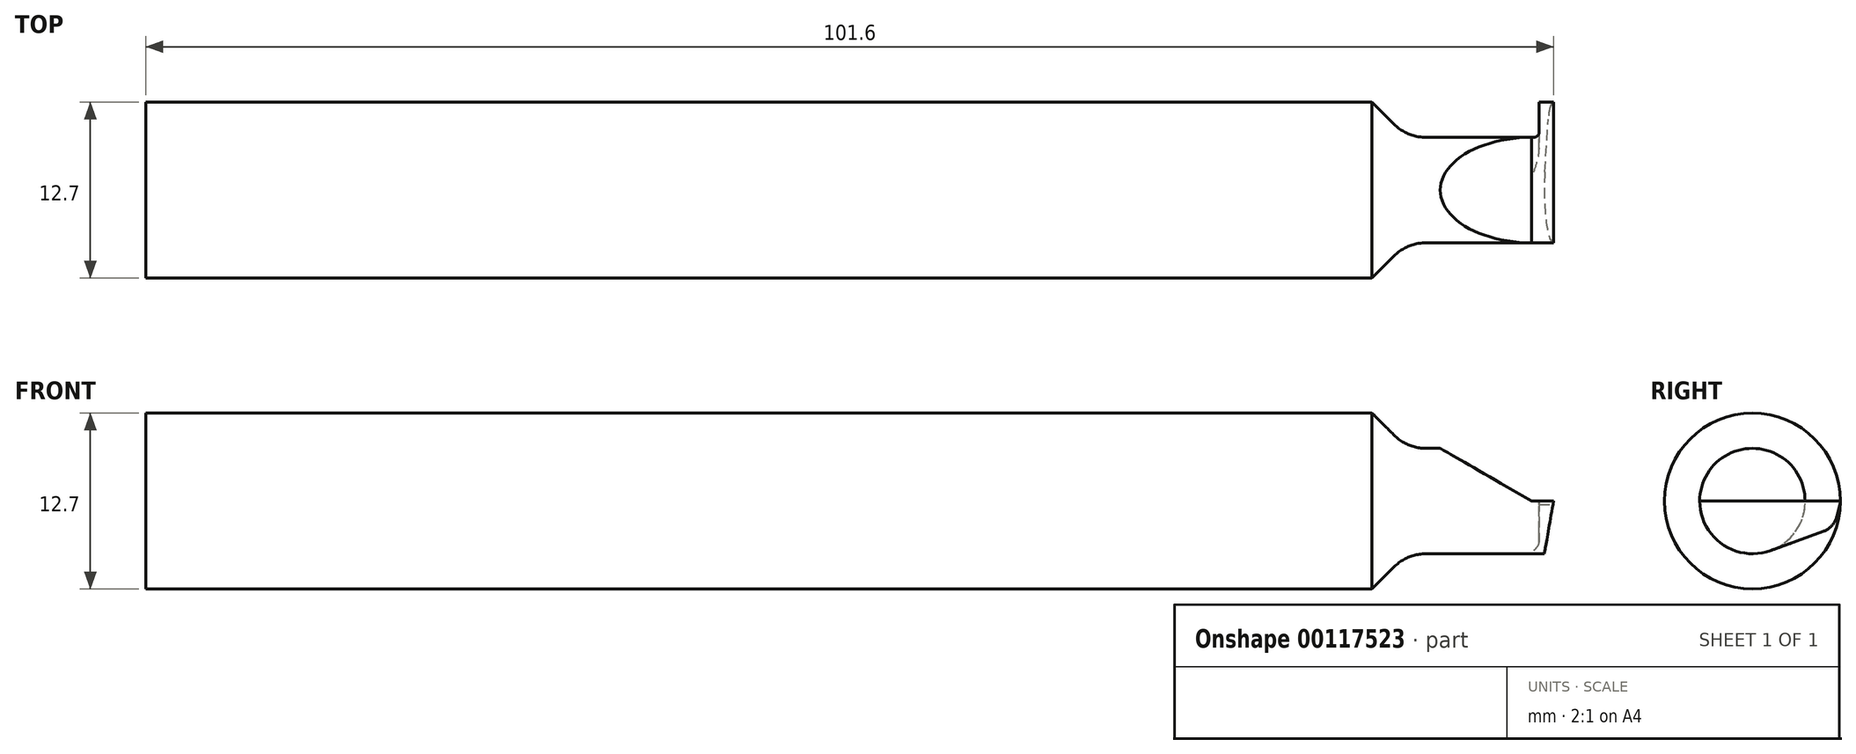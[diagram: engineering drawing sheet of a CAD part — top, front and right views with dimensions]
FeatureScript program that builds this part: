
annotation { "Feature Type Name" : "Feature", "Feature Type Description" : "" }
export const myFeature = defineFeature(function(context is Context, id is Id, definition is map)
    precondition{}
    {
        {
            var Q0;
            Q0=qCreatedBy(makeId("Top.planeOp"),FACE);
            var sketch = newSketch(context, id + "F0", { "sketchPlane" : qUnion([Q0])});
            skLineSegment(sketch, "E0", {"start": v(0, 0) * mm, "end": v(0, 6.35) * mm});
            skLineSegment(sketch, "E1", {"start": v(0, 6.35) * mm, "end": v(-1.04, 6.35) * mm});
            skLineSegment(sketch, "E2", {"start": v(-1.04, 6.35) * mm, "end": v(-1.04, 4.2) * mm});
            skLineSegment(sketch, "E3", {"start": v(-1.42, 3.81) * mm, "end": v(-9.25, 3.81) * mm});
            skLineSegment(sketch, "E4", {"start": v(-11.5, 4.74) * mm, "end": v(-13.1, 6.35) * mm});
            skLineSegment(sketch, "E5", {"start": v(-13.1, 6.35) * mm, "end": v(-101.6, 6.35) * mm});
            skLineSegment(sketch, "E6", {"start": v(-101.6, 6.35) * mm, "end": v(-101.6, 0) * mm});
            skLineSegment(sketch, "E7", {"start": v(-101.6, 0) * mm, "end": v(0, 0) * mm});
            skPoint(sketch, "E8.visualSharp", {"position": v(0, 6.35) * mm});
            skPoint(sketch, "E9.visualSharp", {"position": v(-1.04, 6.35) * mm});
            skPoint(sketch, "E10.visualSharp", {"position": v(-1.04, 3.81) * mm});
            skArc(sketch, "E10.filletArc", {"start": v(-1.42, 3.81) * mm, "mid": v(-1.15, 3.92) * mm, "end": v(-1.04, 4.2) * mm});
            skPoint(sketch, "E11.visualSharp", {"position": v(-10.57, 3.81) * mm});
            skArc(sketch, "E11.filletArc", {"start": v(-11.5, 4.74) * mm, "mid": v(-10.47, 4.05) * mm, "end": v(-9.25, 3.81) * mm});
            skSolve(sketch);
        }
        {
            var Q0;
            Q0=qSketchRegion(id+"F0",true);
            var Q1;
            Q1=sQuery(id+"F0.wireOp",EDGE,"E7");
            revolve(context, id + "F1", {"entities" : qUnion([Q0]), "axis" : qUnion([Q1]), "revolveType" : RevolveType.FULL});
        }
        {
            var Q0;
            Q0=qCreatedBy(makeId("Front.planeOp"),FACE);
            var sketch = newSketch(context, id + "F2", { "sketchPlane" : qUnion([Q0])});
            skLineSegment(sketch, "E12", {"start": v(0, 0) * mm, "end": v(-1.59, 0) * mm});
            skLineSegment(sketch, "E13", {"start": v(-1.59, 0) * mm, "end": v(-12.59, 6.35) * mm});
            skLineSegment(sketch, "E14", {"start": v(-12.59, 6.35) * mm, "end": v(0, 6.35) * mm});
            skLineSegment(sketch, "E15", {"start": v(0, 6.35) * mm, "end": v(0, 0) * mm});
            skSolve(sketch);
        }
        {
            var Q0;
            Q0=qSketchRegion(id+"F2",true);
            extrude(context, id + "F3", {"entities" : qUnion([Q0]), "operationType" : NewBodyOperationType.REMOVE, "endBound" : BoundingType.SYMMETRIC, "oppositeDirection" : true, "depth" : 25.4 * mm});
        }
        {
            var Q0;
            Q0=makeQuery(id+"F1.opRevolve","SWEPT_FACE",FACE,{"disambiguationData":[OSD([sQuery(id+"F0.wireOp",EDGE,"E0")])]});
            var sketch = newSketch(context, id + "F4", { "sketchPlane" : qUnion([Q0])});
            skLineSegment(sketch, "E16", {"start": v(-6.6, -6.6) * mm, "end": v(6.35, -6.6) * mm});
            skLineSegment(sketch, "E17", {"start": v(-3.81, 0) * mm, "end": v(-6.6, 0) * mm});
            skLineSegment(sketch, "E18", {"start": v(-6.6, 0) * mm, "end": v(-6.6, -6.6) * mm});
            skLineSegment(sketch, "E19", {"start": v(1.3, -3.58) * mm, "end": v(5.1, -2.2) * mm});
            skLineSegment(sketch, "E20", {"start": v(6.1, -1.12) * mm, "end": v(6.33, -0.25) * mm});
            skLineSegment(sketch, "E21", {"start": v(6.33, -0.25) * mm, "end": v(6.35, 0) * mm});
            skLineSegment(sketch, "E22", {"start": v(6.35, 0) * mm, "end": v(6.35, -6.6) * mm});
            skArc(sketch, "E23.trimOffspring", {"start": v(1.3, -3.58) * mm, "mid": v(-2.19, -3.12) * mm, "end": v(-3.81, 0) * mm});
            skPoint(sketch, "E24.0.start.orphan", {"position": v(3.81, 0) * mm});
            skPoint(sketch, "E25.orphan", {"position": v(-3.81, 0) * mm});
            skPoint(sketch, "E26.visualSharp", {"position": v(5.88, -1.91) * mm});
            skArc(sketch, "E26.filletArc", {"start": v(5.1, -2.2) * mm, "mid": v(5.73, -1.78) * mm, "end": v(6.1, -1.12) * mm});
            skSolve(sketch);
        }
        {
            var Q0;
            {var subQ1=sQuery(id+"F4.wireOp",EDGE,"E19");Q0=makeQuery(id+"F4.imprint","IMPRINT",FACE,{"disambiguationData":[TD([[makeQuery(id+"F4.imprint","IMPRINT",EDGE,{"derivedFrom":subQ1}),-1.0]])]});}
            var Q1;
            Q1=makeQuery(id+"F4.imprint","IMPRINT",FACE,{"disambiguationData":[TD([[makeQuery(id+"F4.imprint","IMPRINT",EDGE,{"derivedFrom":sQuery(id+"F4.wireOp",EDGE,"E16")}),1.0]])]});
            extrude(context, id + "F5", {"entities" : qUnion([Q0, Q1]), "operationType" : NewBodyOperationType.REMOVE, "oppositeDirection" : true, "depth" : 1.59 * mm});
        }
        {
            var Q0;
            Q0=qCreatedBy(makeId("Front.planeOp"),FACE);
            var sketch = newSketch(context, id + "F6", { "sketchPlane" : qUnion([Q0])});
            skLineSegment(sketch, "E27", {"start": v(0, 0) * mm, "end": v(-0.75, -4.24) * mm});
            skLineSegment(sketch, "E28", {"start": v(-0.75, -4.24) * mm, "end": v(0, -4.24) * mm});
            skLineSegment(sketch, "E29", {"start": v(0, -4.24) * mm, "end": v(0, 0) * mm});
            skSolve(sketch);
        }
        {
            var Q0;
            Q0=qSketchRegion(id+"F6",true);
            extrude(context, id + "F7", {"entities" : qUnion([Q0]), "operationType" : NewBodyOperationType.REMOVE, "endBound" : BoundingType.SYMMETRIC, "oppositeDirection" : true, "depth" : 25.4 * mm});
        }
    });
